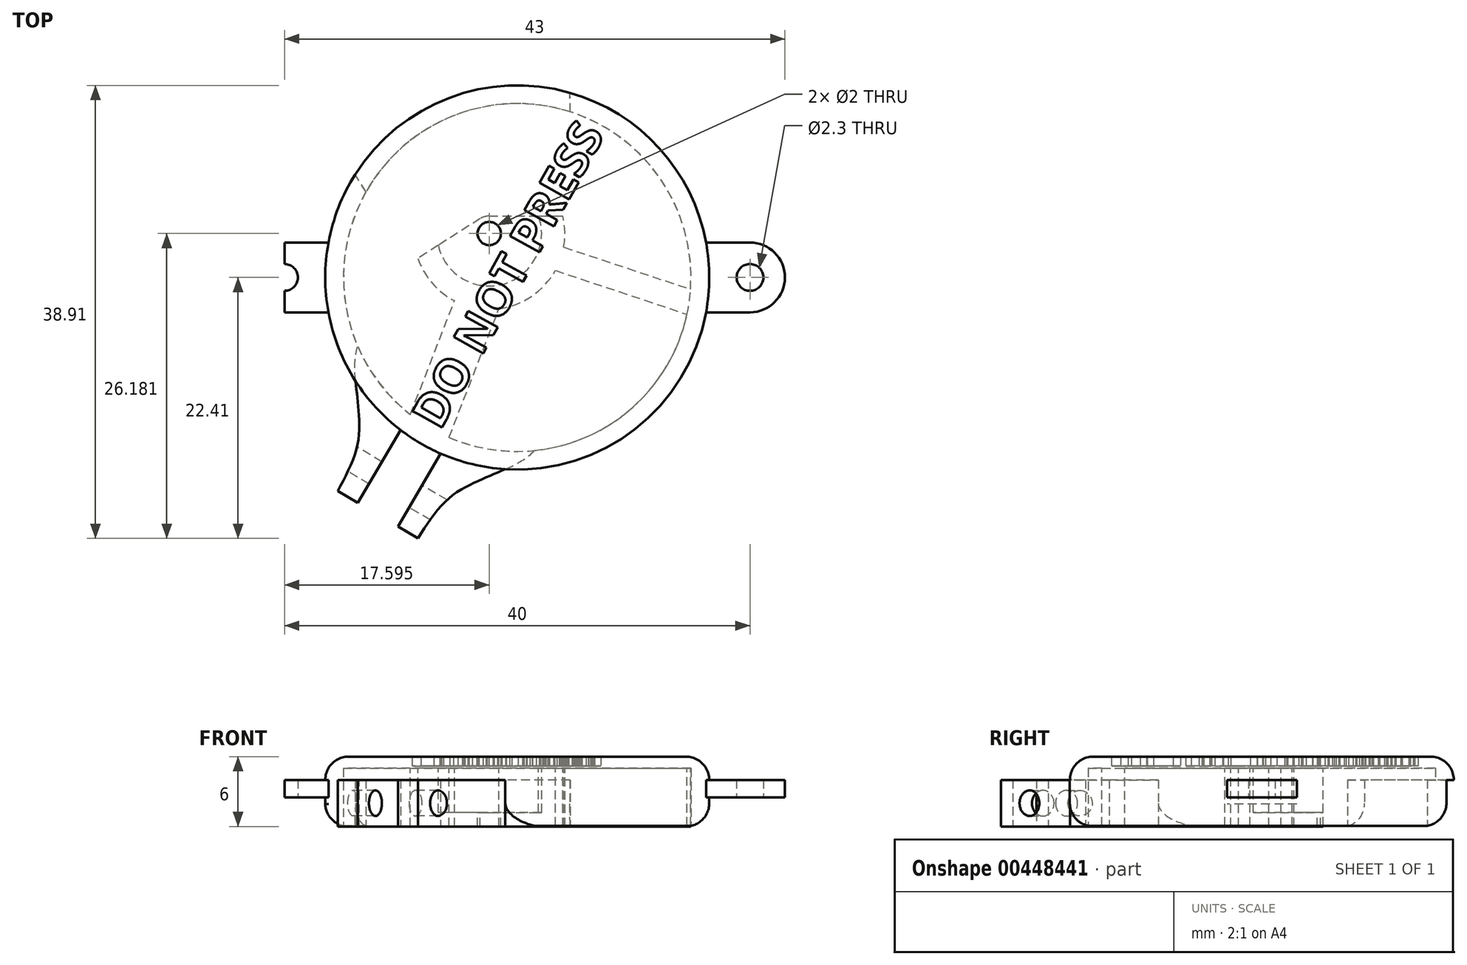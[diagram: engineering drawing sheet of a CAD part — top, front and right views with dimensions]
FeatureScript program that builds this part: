
annotation { "Feature Type Name" : "Feature", "Feature Type Description" : "" }
export const myFeature = defineFeature(function(context is Context, id is Id, definition is map)
    precondition{}
    {
        {
            var Q0;
            Q0=qCreatedBy(makeId("Top.planeOp"),FACE);
            var sketch = newSketch(context, id + "F0", { "sketchPlane" : qUnion([Q0])});
            skCircle(sketch, "E0", {"center": v(0, 0) * mm, "radius": 16.5 * mm});
            skLineSegment(sketch, "E1", {"start": v(0, 0) * mm, "end": v(-16.5, 0) * mm, "construction": true});
            skLineSegment(sketch, "E2", {"start": v(0, 0) * mm, "end": v(-8.87, 13.91) * mm, "construction": true});
            skCircle(sketch, "E3", {"center": v(-2.4, 3.77) * mm, "radius": 1 * mm});
            skLineSegment(sketch, "E4", {"start": v(0, 0) * mm, "end": v(0, 0) * mm});
            skLineSegment(sketch, "E5", {"start": v(0, 0) * mm, "end": v(-8.36, -14.22) * mm, "construction": true});
            skLineSegment(sketch, "E6", {"start": v(-2.4, 3.77) * mm, "end": v(-5.84, 15.43) * mm, "construction": true});
            skLineSegment(sketch, "E7", {"start": v(-2.4, 3.77) * mm, "end": v(-2.47, 16.31) * mm, "construction": true});
            skLineSegment(sketch, "E8", {"start": v(-8.36, -14.22) * mm, "end": v(-10.46, -17.8) * mm, "construction": true});
            skLineSegment(sketch, "E9.0", {"start": v(-6.58, -15.13) * mm, "end": v(-8.74, -18.8) * mm});
            skLineSegment(sketch, "E10", {"start": v(-10.46, -17.8) * mm, "end": v(-8.74, -18.8) * mm});
            skLineSegment(sketch, "E11", {"start": v(-8.74, -18.8) * mm, "end": v(-10.26, -21.4) * mm});
            skPoint(sketch, "E12", {"position": v(-8.23, -17.94) * mm});
            skPoint(sketch, "E13", {"position": v(-9.24, -19.67) * mm});
            skLineSegment(sketch, "E14", {"start": v(-10.26, -21.4) * mm, "end": v(-8.53, -22.4) * mm});
            skFitSpline(sketch, "E15", {"points": [v(-8.53, -22.4) * mm, v(-5.95, -19.04) * mm, v(-3.23, -17.42) * mm, v(-1.03, -16.47) * mm], "startDerivative": vector(6.3, 9.8) * mm, "endDerivative": vector(7.43, 3.2) * mm});
            skLineSegment(sketch, "E16.MirrorCS", {"start": v(-10.03, -13.1) * mm, "end": v(-12.19, -16.78) * mm});
            skLineSegment(sketch, "E17.MirrorCS", {"start": v(-12.19, -16.78) * mm, "end": v(-13.7, -19.36) * mm});
            skLineSegment(sketch, "E18.MirrorCS", {"start": v(-13.7, -19.36) * mm, "end": v(-15.43, -18.35) * mm});
            skFitSpline(sketch, "E19.MirrorCS", {"points": [v(-15.43, -18.35) * mm, v(-13.75, -14.45) * mm, v(-13.65, -11.3) * mm, v(-13.9, -8.9) * mm], "startDerivative": vector(5.5, 10.28) * mm, "endDerivative": vector(-0.82, 8.05) * mm});
            skLineSegment(sketch, "E20.0", {"start": v(4.55, 13.57) * mm, "end": v(4.53, 15.86) * mm});
            skLineSegment(sketch, "E21.0", {"start": v(-12.61, 6.76) * mm, "end": v(-13.94, 8.83) * mm});
            skArc(sketch, "E22", {"start": v(4.55, 13.57) * mm, "mid": v(-5.28, 13.3) * mm, "end": v(-12.61, 6.76) * mm});
            skArc(sketch, "E23", {"start": v(2.08, -13.82) * mm, "mid": v(-7.08, -12.05) * mm, "end": v(-13.09, -4.9) * mm});
            skFitSpline(sketch, "E24", {"points": [v(-1.03, -16.47) * mm, v(2.08, -13.82) * mm], "startDerivative": vector(6.18, 2.48) * mm, "endDerivative": vector(-0.34, 1.45) * mm});
            skFitSpline(sketch, "E25.MirrorCS", {"points": [v(-13.9, -8.9) * mm, v(-13.09, -4.9) * mm], "startDerivative": vector(-0.83, 6.6) * mm, "endDerivative": vector(1.43, 0.4) * mm});
            skSolve(sketch);
        }
        {
            var Q0;
            Q0=qCreatedBy(makeId("Top.planeOp"),FACE);
            var sketch = newSketch(context, id + "F1", { "sketchPlane" : qUnion([Q0])});
            skPoint(sketch, "E26.middle", {"position": v(0, 0) * mm});
            skLineSegment(sketch, "E27.1.0", {"start": v(-20, 3) * mm, "end": v(-16.22, 3) * mm});
            skLineSegment(sketch, "E27.1.1", {"start": v(-20, -3) * mm, "end": v(-16.22, -3) * mm});
            skPoint(sketch, "E28", {"position": v(-20, 0) * mm});
            skLineSegment(sketch, "E29", {"start": v(-20, 3) * mm, "end": v(-20, -3) * mm});
            skArc(sketch, "E30", {"start": v(-20, -3) * mm, "mid": v(-23, 0) * mm, "end": v(-20, 3) * mm});
            skCircle(sketch, "E31", {"center": v(-20, 0) * mm, "radius": 1.15 * mm});
            skLineSegment(sketch, "E32", {"start": v(0, 7.1) * mm, "end": v(0, -5.24) * mm, "construction": true});
            skLineSegment(sketch, "E33.MirrorCS", {"start": v(20, -3) * mm, "end": v(16.22, -3) * mm});
            skArc(sketch, "E34.MirrorCS", {"start": v(20, -3) * mm, "mid": v(23, 0) * mm, "end": v(20, 3) * mm});
            skCircle(sketch, "E35.MirrorC", {"center": v(20, 0) * mm, "radius": 1.15 * mm});
            skLineSegment(sketch, "E36.MirrorCS", {"start": v(20, 3) * mm, "end": v(16.23, 3) * mm});
            skArc(sketch, "E37", {"start": v(-16.22, 3) * mm, "mid": v(-16.5, 0) * mm, "end": v(-16.22, -3) * mm});
            skArc(sketch, "E38", {"start": v(16.23, 3) * mm, "mid": v(16.5, 0) * mm, "end": v(16.22, -3) * mm});
            skSolve(sketch);
        }
        {
            var Q0;
            Q0=makeQuery(id+"F0.imprint","IMPRINT",FACE,{"disambiguationData":[TD([[makeQuery(id+"F0.imprint","IMPRINT",EDGE,{"derivedFrom":sQuery(id+"F0.wireOp",EDGE,"E0")}),1.0]])]});
            var Q1;
            {var subQ0=sQuery(id+"F0.wireOp",EDGE,"E20.0");Q1=makeQuery(id+"F0.imprint","IMPRINT",FACE,{"disambiguationData":[TD([[makeQuery(id+"F0.imprint","IMPRINT",EDGE,{"derivedFrom":subQ0}),1.0]])]});}
            var Q2;
            Q2=makeQuery(id+"F0.imprint","IMPRINT",FACE,{"disambiguationData":[TD([[makeQuery(id+"F0.imprint","IMPRINT",EDGE,{"derivedFrom":sQuery(id+"F0.wireOp",EDGE,"E3")}),-1.0]])]});
            extrude(context, id + "F2", {"entities" : qUnion([Q0, Q1, Q2]), "depth" : 6 * mm, "offsetDistance" : 25.4 * mm});
        }
        {
            var Q0;
            {var subQ0=sQuery(id+"F1.wireOp",EDGE,"b84d2e20-32c3-4111-8ed6-a1b564a6f677");Q0=makeQuery(id+"F1.imprint","IMPRINT",FACE,{"disambiguationData":[TD([[makeQuery(id+"F1.imprint","IMPRINT",EDGE,{"derivedFrom":subQ0}),1.0]])]});}
            var Q1;
            {var subQ3=sQuery(id+"F1.wireOp",EDGE,"NuOv7suO-u1RK-2Ga4-L83Y-BCEB7LIjCZRI.left");Q1=makeQuery(id+"F1.imprint","IMPRINT",FACE,{"disambiguationData":[TD([[makeQuery(id+"F1.imprint","IMPRINT",EDGE,{"derivedFrom":subQ3}),1.0]])]});}
            var Q2;
            {var subQ0=sQuery(id+"F1.wireOp",EDGE,"b84d2e20-32c3-4111-8ed6-a1b564a6f677");Q2=makeQuery(id+"F1.imprint","IMPRINT",FACE,{"disambiguationData":[TD([[makeQuery(id+"F1.imprint","IMPRINT",EDGE,{"derivedFrom":subQ0}),-1.0]])]});}
            var Q3;
            {var subQ0=sQuery(id+"F1.wireOp",EDGE,"E27.3.2");Q3=makeQuery(id+"F1.imprint","IMPRINT",FACE,{"disambiguationData":[TD([[makeQuery(id+"F1.imprint","IMPRINT",EDGE,{"derivedFrom":subQ0}),1.0]])]});}
            var Q4;
            Q4=makeQuery(id+"F0.imprint","IMPRINT",FACE,{"disambiguationData":[TD([[makeQuery(id+"F0.imprint","IMPRINT",EDGE,{"derivedFrom":sQuery(id+"F0.wireOp",EDGE,"E0")}),1.0]])]});
            var Q5;
            {var subQ0=sQuery(id+"F1.wireOp",EDGE,"E27.2.2");Q5=makeQuery(id+"F1.imprint","IMPRINT",FACE,{"disambiguationData":[TD([[makeQuery(id+"F1.imprint","IMPRINT",EDGE,{"derivedFrom":subQ0}),1.0]])]});}
            var Q6;
            {var subQ0=sQuery(id+"F1.wireOp",EDGE,"E27.1.2");Q6=makeQuery(id+"F1.imprint","IMPRINT",FACE,{"disambiguationData":[TD([[makeQuery(id+"F1.imprint","IMPRINT",EDGE,{"derivedFrom":subQ0}),1.0]])]});}
            extrude(context, id + "F3", {"entities" : qUnion([Q0, Q1, Q2, Q3, Q4, Q5, Q6]), "operationType" : NewBodyOperationType.ADD, "depth" : 4 * mm, "offsetDistance" : 25 * mm});
        }
        {
            var Q0;
            Q0=makeQuery(id+"F2.opExtrude","CAP_EDGE",EDGE,{"disambiguationData":[OSD([sQuery(id+"F0.wireOp",EDGE,"E0")])],"isStart":false});
            var Q1;
            {var subQ1=sQuery(id+"F0.wireOp",EDGE,"E0");var subQ2=sQuery(id+"F1.wireOp",EDGE,"E27.1.1");var subQ3=sQuery(id+"F1.wireOp",EDGE,"NuOv7suO-u1RK-2Ga4-L83Y-BCEB7LIjCZRI.bottom");Q1=makeQuery(id+"F3.boolean.opBoolean","SPLIT",EDGE,{"disambiguationData":[TD([makeQuery(id+"F3.opExtrude","SWEPT_FACE",FACE,{"disambiguationData":[OSD([subQ3,subQ2])]})])],"derivedFrom":makeQuery(id+"F2.opExtrude","CAP_EDGE",EDGE,{"disambiguationData":[OSD([subQ1])],"isStart":true})});}
            var Q2;
            {var subQ1=sQuery(id+"F0.wireOp",EDGE,"E0");var subQ2=sQuery(id+"F1.wireOp",EDGE,"E27.1.0");var subQ3=sQuery(id+"F1.wireOp",EDGE,"NuOv7suO-u1RK-2Ga4-L83Y-BCEB7LIjCZRI.top");Q2=makeQuery(id+"F3.boolean.opBoolean","SPLIT",EDGE,{"disambiguationData":[TD([makeQuery(id+"F3.opExtrude","SWEPT_FACE",FACE,{"disambiguationData":[OSD([subQ3,subQ2])]})])],"derivedFrom":makeQuery(id+"F2.opExtrude","CAP_EDGE",EDGE,{"disambiguationData":[OSD([subQ1])],"isStart":true})});}
            fillet(context, id + "F4", {"entities" : qUnion([Q0, Q1, Q2]), "radius" : 2 * mm, "tangentPropagation" : true, "allowEdgeOverflow" : false});
        }
        {
            var Q0;
            Q0=makeQuery(id+"F0.imprint","IMPRINT",FACE,{"disambiguationData":[TD([[makeQuery(id+"F0.imprint","IMPRINT",EDGE,{"derivedFrom":sQuery(id+"F0.wireOp",EDGE,"E0")}),1.0]])]});
            var sketch = newSketch(context, id + "F5", { "sketchPlane" : qUnion([Q0])});
            skCircle(sketch, "E39", {"center": v(0, 0) * mm, "radius": 14.93 * mm});
            skSolve(sketch);
        }
        {
            var Q0;
            Q0=makeQuery(id+"F5.imprint","IMPRINT",FACE,{"disambiguationData":[TD([[makeQuery(id+"F5.imprint","IMPRINT",EDGE,{"derivedFrom":sQuery(id+"F5.wireOp",EDGE,"E39")}),1.0]])]});
            var Q1;
            Q1=makeQuery(id+"F5.imprint","IMPRINT",FACE,{"disambiguationData":[TD([[makeQuery(id+"F5.imprint","IMPRINT",EDGE,{"derivedFrom":makeQuery(id+"F0.imprint","IMPRINT",EDGE,{"derivedFrom":sQuery(id+"F0.wireOp",EDGE,"E3")})}),-1.0]])]});
            extrude(context, id + "F6", {"entities" : qUnion([Q0, Q1]), "operationType" : NewBodyOperationType.REMOVE, "depth" : 5 * mm, "offsetDistance" : 25 * mm});
        }
        {
            var Q0;
            {var subQ0=sQuery(id+"F0.wireOp",EDGE,"E16.MirrorCS");Q0=makeQuery(id+"F0.imprint","IMPRINT",FACE,{"disambiguationData":[TD([[makeQuery(id+"F0.imprint","IMPRINT",EDGE,{"derivedFrom":subQ0}),-1.0]])]});}
            var Q1;
            {var subQ0=sQuery(id+"F0.wireOp",EDGE,"E9.0");Q1=makeQuery(id+"F0.imprint","IMPRINT",FACE,{"disambiguationData":[TD([[makeQuery(id+"F0.imprint","IMPRINT",EDGE,{"derivedFrom":subQ0}),1.0]])]});}
            var Q2;
            {var subQ2=sQuery(id+"F1.wireOp",EDGE,"E27.1.0");Q2=makeQuery(id+"F1.imprint","IMPRINT",FACE,{"disambiguationData":[TD([[makeQuery(id+"F1.imprint","IMPRINT",EDGE,{"derivedFrom":subQ2}),-1.0]])]});}
            var Q3;
            {var subQ0=sQuery(id+"F1.wireOp",EDGE,"E30");Q3=makeQuery(id+"F1.imprint","IMPRINT",FACE,{"disambiguationData":[TD([[makeQuery(id+"F1.imprint","IMPRINT",EDGE,{"derivedFrom":subQ0}),-1.0]])]});}
            var Q4;
            Q4=makeQuery(id+"F1.imprint","IMPRINT",FACE,{"disambiguationData":[TD([[makeQuery(id+"F1.imprint","IMPRINT",EDGE,{"derivedFrom":sQuery(id+"F1.wireOp",EDGE,"E33.MirrorCS")}),-1.0]])]});
            var Q5;
            {var subQ2=sQuery(id+"F0.wireOp",EDGE,"E24");var subQ7=sQuery(id+"F5.wireOp",EDGE,"E39");var subQ8=makeQuery(id+"F0.imprint","IMPRINT",EDGE,{"derivedFrom":subQ2});var subQ9=makeQuery(id+"F5.imprint","INTERSECT",VERTEX,{"derivedFrom":[subQ8,subQ7]});Q5=makeQuery(id+"F5.imprint","IMPRINT",FACE,{"disambiguationData":[TD([[makeQuery(id+"F5.imprint","IMPRINT",EDGE,{"disambiguationData":[TD([[subQ9,1.0]])],"derivedFrom":subQ7}),-1.0]])]});}
            extrude(context, id + "F7", {"entities" : qUnion([Q0, Q1, Q2, Q3, Q4, Q5]), "operationType" : NewBodyOperationType.ADD, "depth" : 4 * mm, "offsetDistance" : 25 * mm});
        }
        {
            var Q0;
            Q0=makeQuery(id+"F7.opExtrude","SWEPT_FACE",FACE,{"disambiguationData":[OSD([sQuery(id+"F0.wireOp",EDGE,"E9.0"),sQuery(id+"F0.wireOp",EDGE,"E11")])]});
            var sketch = newSketch(context, id + "F8", { "sketchPlane" : qUnion([Q0])});
            skPoint(sketch, "E40", {"position": v(20.64, 0) * mm});
            skCircle(sketch, "E41", {"center": v(20.64, 2) * mm, "radius": 1.1 * mm});
            skSolve(sketch);
        }
        {
            var Q0;
            Q0=makeQuery(id+"F8.imprint","IMPRINT",FACE,{"disambiguationData":[TD([[makeQuery(id+"F8.imprint","IMPRINT",EDGE,{"derivedFrom":sQuery(id+"F8.wireOp",EDGE,"E41")}),1.0]])]});
            extrude(context, id + "F9", {"entities" : qUnion([Q0]), "operationType" : NewBodyOperationType.REMOVE, "oppositeDirection" : true, "depth" : 25 * mm, "offsetDistance" : 25 * mm, "symmetric" : true});
        }
        {
            var Q0;
            {var subQ0=sQuery(id+"F1.wireOp",EDGE,"E30");Q0=makeQuery(id+"F1.imprint","IMPRINT",FACE,{"disambiguationData":[TD([[makeQuery(id+"F1.imprint","IMPRINT",EDGE,{"derivedFrom":subQ0}),-1.0]])]});}
            var Q1;
            {var subQ2=sQuery(id+"F1.wireOp",EDGE,"E27.1.0");Q1=makeQuery(id+"F1.imprint","IMPRINT",FACE,{"disambiguationData":[TD([[makeQuery(id+"F1.imprint","IMPRINT",EDGE,{"derivedFrom":subQ2}),-1.0]])]});}
            var Q2;
            Q2=makeQuery(id+"F1.imprint","IMPRINT",FACE,{"disambiguationData":[TD([[makeQuery(id+"F1.imprint","IMPRINT",EDGE,{"derivedFrom":sQuery(id+"F1.wireOp",EDGE,"E33.MirrorCS")}),-1.0]])]});
            extrude(context, id + "F10", {"entities" : qUnion([Q0, Q1, Q2]), "operationType" : NewBodyOperationType.REMOVE, "depth" : 2.5 * mm, "offsetDistance" : 25 * mm});
        }
        {
            var Q0;
            {var subQ0=sQuery(id+"F0.wireOp",EDGE,"E20.0");Q0=makeQuery(id+"F0.imprint","IMPRINT",FACE,{"disambiguationData":[TD([[makeQuery(id+"F0.imprint","IMPRINT",EDGE,{"derivedFrom":subQ0}),1.0]])]});}
            extrude(context, id + "F11", {"entities" : qUnion([Q0]), "operationType" : NewBodyOperationType.REMOVE, "depth" : 4 * mm, "offsetDistance" : 25 * mm});
        }
        {
            var Q0;
            Q0=makeQuery(id+"F6.boolean.opBoolean","COPY",FACE,{"derivedFrom":makeQuery(id+"F6.opExtrude","CAP_FACE",FACE,{"disambiguationData":[OSD([sQuery(id+"F5.wireOp",EDGE,"E39")])],"isStart":false})});
            var sketch = newSketch(context, id + "F12", { "sketchPlane" : qUnion([Q0])});
            skCircle(sketch, "E42", {"center": v(-2.4, -3.77) * mm, "radius": 4.5 * mm});
            skLineSegment(sketch, "E43", {"start": v(-2.4, -5.27) * mm, "end": v(1.84, -5.27) * mm});
            skLineSegment(sketch, "E44", {"start": v(-2.4, -3.77) * mm, "end": v(-3.21, -5.04) * mm});
            skLineSegment(sketch, "E45", {"start": v(-3.21, -5.04) * mm, "end": v(-3.21, -5.04) * mm});
            skLineSegment(sketch, "E46", {"start": v(-3.21, -5.04) * mm, "end": v(-6.79, -2.76) * mm});
            skArc(sketch, "E47", {"start": v(-2.4, -5.27) * mm, "mid": v(-2.83, -5.21) * mm, "end": v(-3.21, -5.04) * mm});
            skPoint(sketch, "E48.orphan", {"position": v(-6.65, -5.27) * mm});
            skCircle(sketch, "E49", {"center": v(-2.4, -3.77) * mm, "radius": 6.5 * mm});
            skLineSegment(sketch, "E50", {"start": v(1.84, -5.27) * mm, "end": v(3.92, -5.27) * mm});
            skLineSegment(sketch, "E51", {"start": v(-6.79, -2.76) * mm, "end": v(-8.54, -1.64) * mm});
            skLineSegment(sketch, "E52", {"start": v(-9.18, 11.78) * mm, "end": v(-5.4, 2) * mm});
            skLineSegment(sketch, "E53", {"start": v(-5.85, 13.74) * mm, "end": v(-1.57, 2.67) * mm});
            skLineSegment(sketch, "E54", {"start": v(3.27, -0.6) * mm, "end": v(14.6, 3.16) * mm});
            skLineSegment(sketch, "E55", {"start": v(3.99, -2.6) * mm, "end": v(14.9, 1.02) * mm});
            skSolve(sketch);
        }
        {
            var Q0;
            {var subQ0=sQuery(id+"F12.wireOp",EDGE,"E50");Q0=makeQuery(id+"F12.imprint","IMPRINT",FACE,{"disambiguationData":[TD([[makeQuery(id+"F12.imprint","IMPRINT",EDGE,{"derivedFrom":subQ0}),1.0]])]});}
            var Q1;
            {var subQ0=sQuery(id+"F12.wireOp",EDGE,"E52");Q1=makeQuery(id+"F12.imprint","IMPRINT",FACE,{"disambiguationData":[TD([[makeQuery(id+"F12.imprint","IMPRINT",EDGE,{"derivedFrom":subQ0}),1.0]])]});}
            var Q2;
            {var subQ0=sQuery(id+"F12.wireOp",EDGE,"E54");Q2=makeQuery(id+"F12.imprint","IMPRINT",FACE,{"disambiguationData":[TD([[makeQuery(id+"F12.imprint","IMPRINT",EDGE,{"derivedFrom":subQ0}),-1.0]])]});}
            extrude(context, id + "F13", {"entities" : qUnion([Q0, Q1, Q2]), "operationType" : NewBodyOperationType.ADD, "depth" : 3.8 * mm, "offsetDistance" : 25 * mm});
        }
        {
            var Q0;
            Q0=makeQuery(id+"F13.opExtrude","CAP_FACE",FACE,{"disambiguationData":[OSD([sQuery(id+"F12.wireOp",EDGE,"E42"),sQuery(id+"F12.wireOp",EDGE,"E49"),sQuery(id+"F12.wireOp",EDGE,"E50"),sQuery(id+"F12.wireOp",EDGE,"E51")])],"isStart":false});
            var sketch = newSketch(context, id + "F14", { "sketchPlane" : qUnion([Q0])});
            skArc(sketch, "E56", {"start": v(-3.18, -5.06) * mm, "mid": v(-2.8, -5.22) * mm, "end": v(-2.4, -5.27) * mm});
            skLineSegment(sketch, "E57", {"start": v(-2.4, -5.27) * mm, "end": v(3.92, -5.27) * mm});
            skLineSegment(sketch, "E58", {"start": v(-3.18, -5.06) * mm, "end": v(-8.54, -1.64) * mm});
            skCircle(sketch, "E59", {"center": v(-2.4, -3.77) * mm, "radius": 1 * mm});
            skSolve(sketch);
        }
        {
            var Q0;
            {var subQ1=makeQuery(id+"F13.opExtrude","CAP_EDGE",EDGE,{"disambiguationData":[OSD([sQuery(id+"F12.wireOp",EDGE,"E42")])],"isStart":false});Q0=makeQuery(id+"F14.imprint","IMPRINT",FACE,{"disambiguationData":[TD([[makeQuery(id+"F14.imprint","IMPRINT",EDGE,{"derivedFrom":subQ1}),-1.0]])]});}
            var Q1;
            {var subQ0=sQuery(id+"F14.wireOp",EDGE,"E56");Q1=makeQuery(id+"F14.imprint","IMPRINT",FACE,{"disambiguationData":[TD([[makeQuery(id+"F14.imprint","IMPRINT",EDGE,{"derivedFrom":subQ0}),1.0]])]});}
            extrude(context, id + "F15", {"entities" : qUnion([Q0, Q1]), "operationType" : NewBodyOperationType.ADD, "depth" : 1.2 * mm, "offsetDistance" : 25 * mm});
        }
        {
            var Q0;
            Q0=makeQuery(id+"F2.opExtrude","CAP_FACE",FACE,{"disambiguationData":[OSD([sQuery(id+"F0.wireOp",EDGE,"E0"),sQuery(id+"F0.wireOp",EDGE,"E3")])],"isStart":false});
            var sketch = newSketch(context, id + "F16", { "sketchPlane" : qUnion([Q0])});
            skText(sketch, "E60", { "text": "DO NOT PRESS", "fontName": "OpenSans-Bold.ttf"});
            const initialGuessF16  = {"E60": [-0.00664, -0.0132, 0.48664, 0.8736, 0.00292]};
            skSetInitialGuess(sketch, initialGuessF16);
            skSolve(sketch);
        }
        {
            var Q0;
            Q0 = qSketchRegion(id + "F16", true);
            extrude(context, id + "F17", {"entities" : qUnion([Q0]), "operationType" : NewBodyOperationType.REMOVE, "oppositeDirection" : true, "depth" : 0.8 * mm, "offsetDistance" : 25 * mm});
        }
    });
